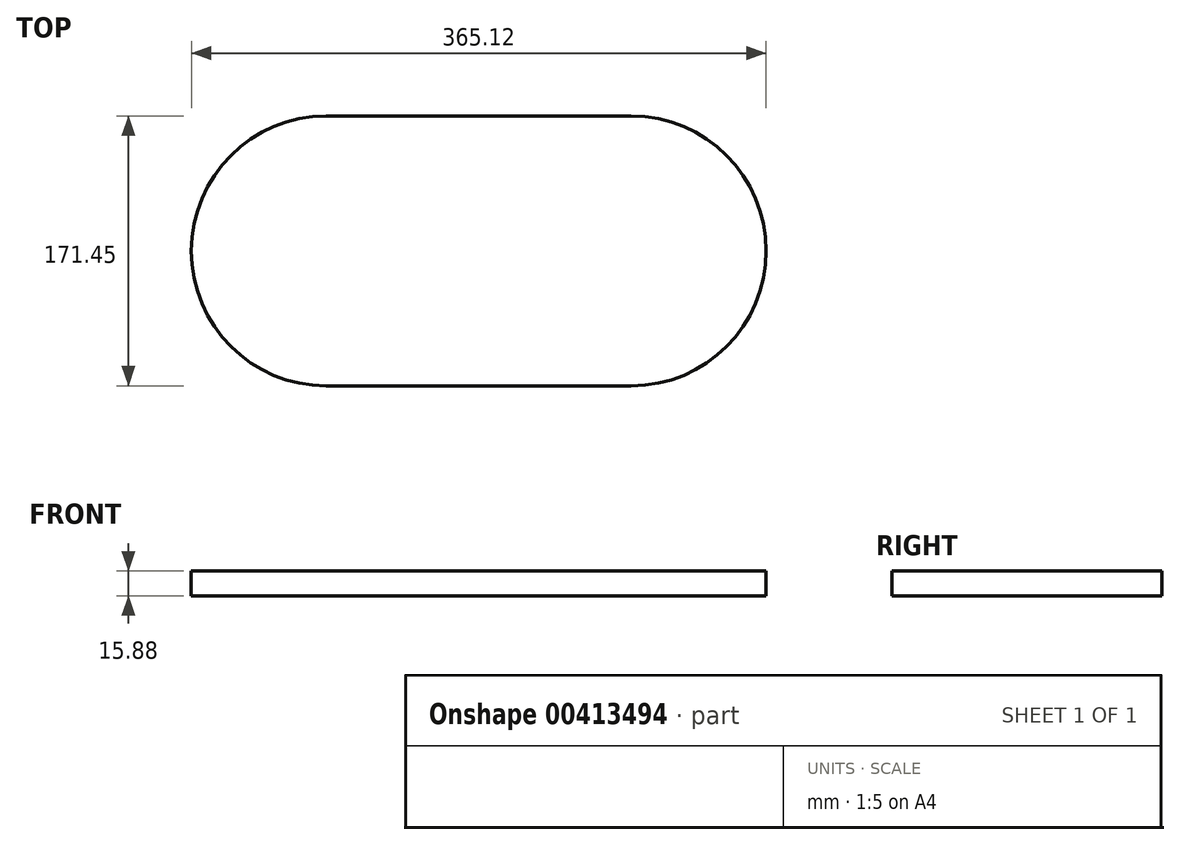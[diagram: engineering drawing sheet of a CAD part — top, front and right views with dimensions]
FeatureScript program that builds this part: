
annotation { "Feature Type Name" : "Feature", "Feature Type Description" : "" }
export const myFeature = defineFeature(function(context is Context, id is Id, definition is map)
    precondition{}
    {
        {
            var Q0;
            Q0=qCreatedBy(makeId("Top.planeOp"),FACE);
            var sketch = newSketch(context, id + "F0", { "sketchPlane" : qUnion([Q0])});
            skPoint(sketch, "E0.middle", {"position": v(0, 0) * mm});
            skLineSegment(sketch, "E1.0", {"start": v(96.84, 85.72) * mm, "end": v(-96.84, 85.73) * mm});
            skLineSegment(sketch, "E2.0", {"start": v(96.84, -85.72) * mm, "end": v(-96.84, -85.73) * mm});
            skLineSegment(sketch, "E3", {"start": v(-182.56, 0) * mm, "end": v(182.56, 0) * mm});
            skPoint(sketch, "E4", {"position": v(-96.84, 0) * mm});
            skPoint(sketch, "E5", {"position": v(96.84, 0) * mm});
            skArc(sketch, "E6", {"start": v(-96.84, -85.73) * mm, "mid": v(-182.56, 0) * mm, "end": v(-96.84, 85.73) * mm});
            skArc(sketch, "E7", {"start": v(96.84, 85.72) * mm, "mid": v(182.56, 0) * mm, "end": v(96.84, -85.72) * mm});
            skSolve(sketch);
        }
        {
            var Q0;
            Q0 = qSketchRegion(id + "F0", true);
            extrude(context, id + "F1", {"entities" : qUnion([Q0]), "depth" : 15.88 * mm});
        }
    });
